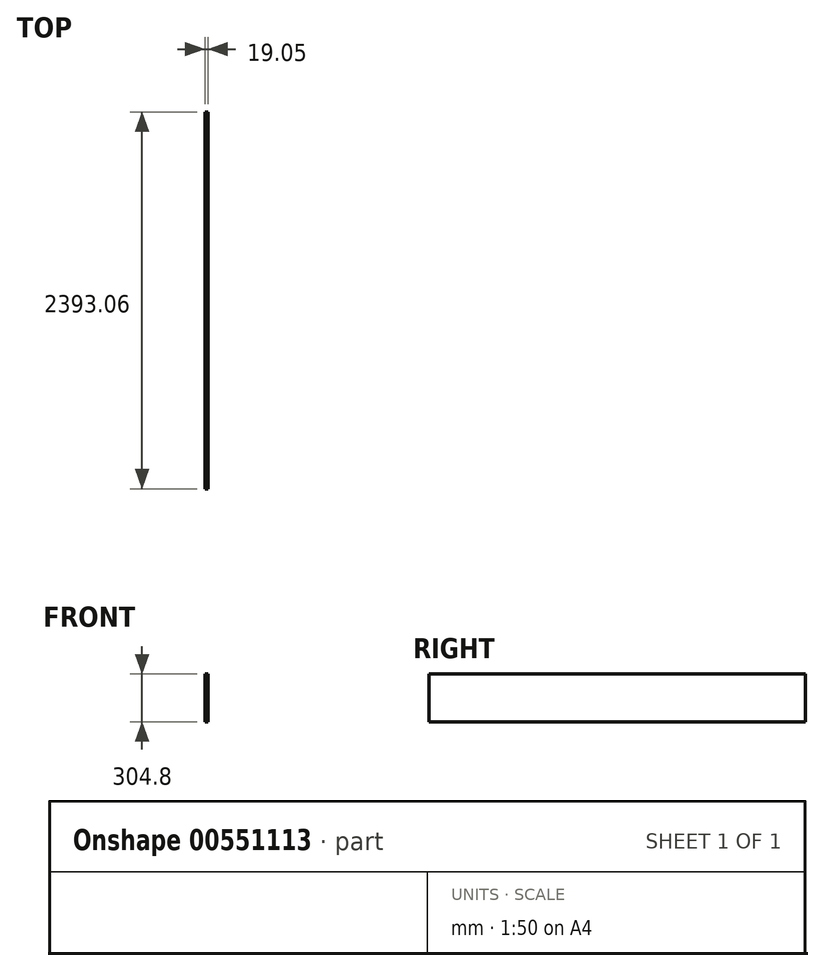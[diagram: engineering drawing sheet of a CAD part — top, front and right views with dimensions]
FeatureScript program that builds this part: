
annotation { "Feature Type Name" : "Feature", "Feature Type Description" : "" }
export const myFeature = defineFeature(function(context is Context, id is Id, definition is map)
    precondition{}
    {
        {
            var Q0;
            Q0=qCreatedBy(makeId("Right.planeOp"),FACE);
            var sketch = newSketch(context, id + "F0", { "sketchPlane" : qUnion([Q0])});
            skLineSegment(sketch, "E0.bottom", {"start": v(1044.13, 152.4) * mm, "end": v(-1044.13, 152.4) * mm});
            skLineSegment(sketch, "E0.top", {"start": v(1044.13, -152.4) * mm, "end": v(-1044.13, -152.4) * mm});
            skLineSegment(sketch, "E0.left", {"start": v(1044.13, 152.4) * mm, "end": v(1044.13, -152.4) * mm});
            skLineSegment(sketch, "E0.right", {"start": v(-1044.13, 152.4) * mm, "end": v(-1044.13, -152.4) * mm});
            skPoint(sketch, "E0.middle", {"position": v(0, 0) * mm});
            skSolve(sketch);
        }
        {
            var Q0;
            Q0=makeQuery(id+"F0.imprint","IMPRINT",FACE,{"disambiguationData":[TD([[makeQuery(id+"F0.imprint","IMPRINT",EDGE,{"derivedFrom":sQuery(id+"F0.wireOp",EDGE,"E0.bottom")}),1.0]])]});
            extrude(context, id + "F1", {"entities" : qUnion([Q0]), "depth" : 19.05 * mm, "offsetDistance" : 25.4 * mm});
        }
        {
            var Q0;
            Q0=makeQuery(id+"F1.opExtrude","SWEPT_FACE",FACE,{"disambiguationData":[OSD([sQuery(id+"F0.wireOp",EDGE,"E0.right")])]});
            extrude(context, id + "F2", {"entities" : qUnion([Q0]), "operationType" : NewBodyOperationType.ADD, "depth" : 304.8 * mm, "offsetDistance" : 25.4 * mm});
        }
    });
